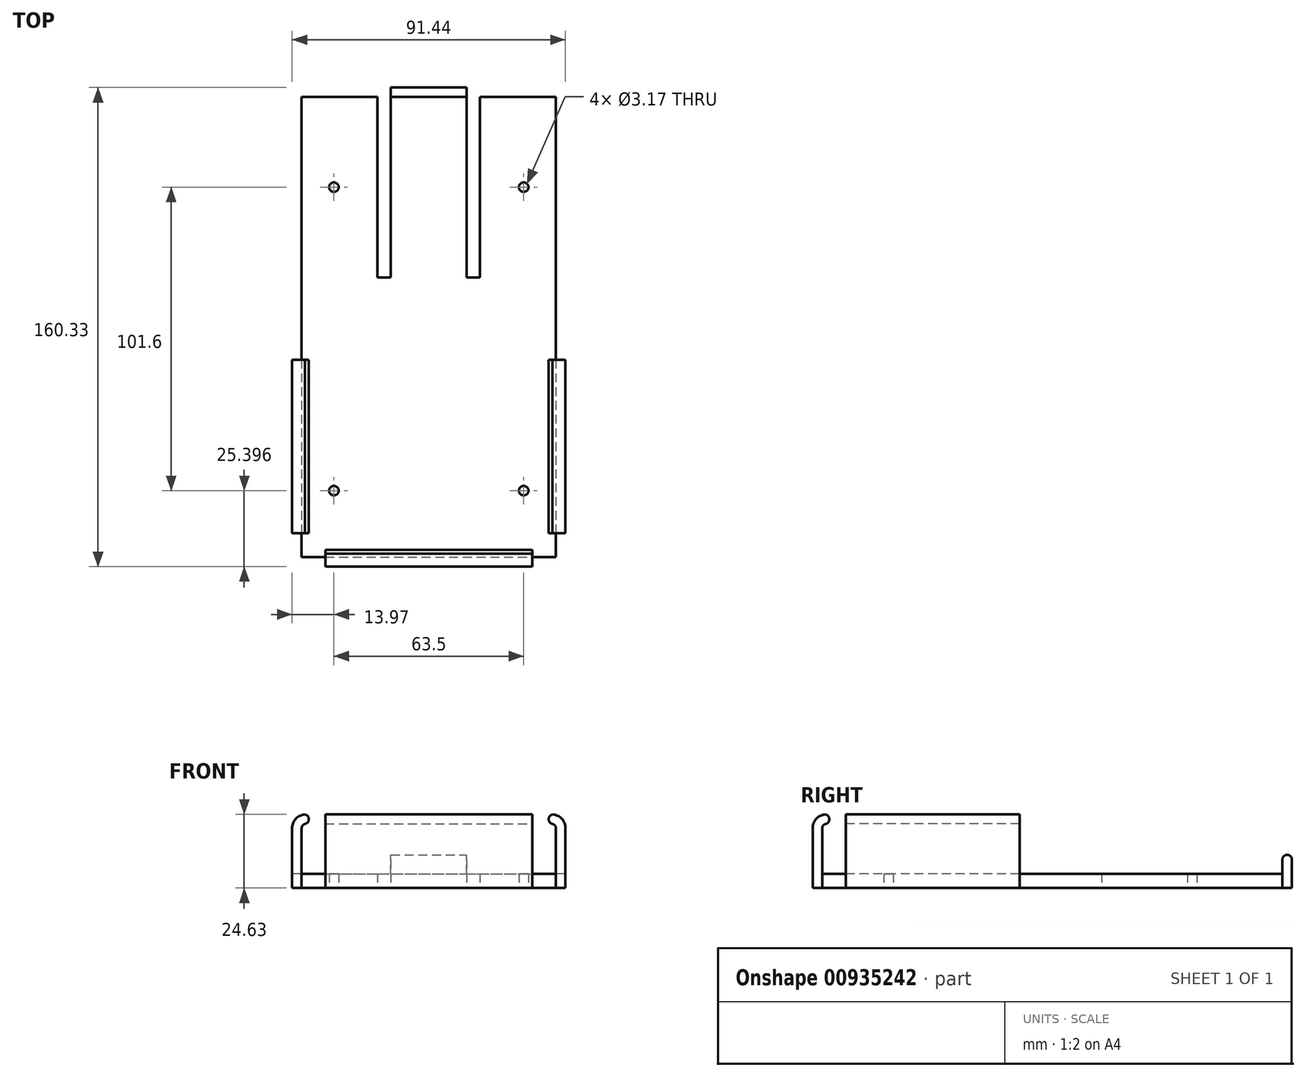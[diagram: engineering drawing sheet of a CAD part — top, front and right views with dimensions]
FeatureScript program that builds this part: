
annotation { "Feature Type Name" : "Feature", "Feature Type Description" : "" }
export const myFeature = defineFeature(function(context is Context, id is Id, definition is map)
    precondition{}
    {
        {
            var Q0;
            Q0=qCreatedBy(makeId("Top.planeOp"),FACE);
            var sketch = newSketch(context, id + "F0", { "sketchPlane" : qUnion([Q0])});
            skLineSegment(sketch, "E0.bottom", {"start": v(-42.54, 87.9) * mm, "end": v(-17.14, 87.9) * mm});
            skLineSegment(sketch, "E0.left", {"start": v(-42.54, 87.9) * mm, "end": v(-42.55, 0) * mm});
            skLineSegment(sketch, "E0.right", {"start": v(42.55, 87.9) * mm, "end": v(42.55, 0) * mm});
            skLineSegment(sketch, "E1", {"start": v(-42.55, 0) * mm, "end": v(-45.72, 0) * mm});
            skLineSegment(sketch, "E2", {"start": v(-45.72, 0) * mm, "end": v(-45.72, -58.15) * mm});
            skLineSegment(sketch, "E3", {"start": v(-45.72, -58.15) * mm, "end": v(-42.54, -58.15) * mm});
            skLineSegment(sketch, "E4", {"start": v(-34.6, -66.09) * mm, "end": v(-34.6, -69.26) * mm});
            skLineSegment(sketch, "E5", {"start": v(-34.6, -69.26) * mm, "end": v(34.6, -69.26) * mm});
            skLineSegment(sketch, "E6", {"start": v(34.6, -69.26) * mm, "end": v(34.6, -66.09) * mm});
            skLineSegment(sketch, "E7", {"start": v(42.54, -58.15) * mm, "end": v(45.72, -58.15) * mm});
            skLineSegment(sketch, "E8", {"start": v(45.72, -58.15) * mm, "end": v(45.72, 0) * mm});
            skLineSegment(sketch, "E9", {"start": v(45.72, 0) * mm, "end": v(42.55, 0) * mm});
            skLineSegment(sketch, "E10", {"start": v(-17.14, 87.9) * mm, "end": v(-17.15, 27.49) * mm});
            skLineSegment(sketch, "E11", {"start": v(-17.15, 27.49) * mm, "end": v(-12.7, 27.49) * mm});
            skLineSegment(sketch, "E12", {"start": v(17.15, 27.49) * mm, "end": v(17.15, 87.9) * mm});
            skLineSegment(sketch, "E13.trimOffspring", {"start": v(17.14, 87.9) * mm, "end": v(42.54, 87.9) * mm});
            skLineSegment(sketch, "E14", {"start": v(-12.7, 27.49) * mm, "end": v(-12.7, 91.07) * mm});
            skLineSegment(sketch, "E15", {"start": v(-12.7, 91.07) * mm, "end": v(12.7, 91.07) * mm});
            skLineSegment(sketch, "E16", {"start": v(12.7, 91.07) * mm, "end": v(12.7, 27.49) * mm});
            skLineSegment(sketch, "E17.trimOffspring", {"start": v(12.7, 27.49) * mm, "end": v(17.15, 27.49) * mm});
            skCircle(sketch, "E18", {"center": v(-31.75, -43.86) * mm, "radius": 1.59 * mm});
            skCircle(sketch, "E19", {"center": v(31.75, -43.86) * mm, "radius": 1.59 * mm});
            skCircle(sketch, "E20", {"center": v(31.75, 57.74) * mm, "radius": 1.59 * mm});
            skCircle(sketch, "E21", {"center": v(-31.75, 57.74) * mm, "radius": 1.59 * mm});
            skLineSegment(sketch, "E22", {"start": v(-42.54, -58.15) * mm, "end": v(-42.54, -66.09) * mm});
            skLineSegment(sketch, "E23", {"start": v(-42.54, -66.09) * mm, "end": v(-34.6, -66.09) * mm});
            skLineSegment(sketch, "E24", {"start": v(42.54, -58.15) * mm, "end": v(42.54, -66.09) * mm});
            skLineSegment(sketch, "E25", {"start": v(42.54, -66.09) * mm, "end": v(34.6, -66.09) * mm});
            skSolve(sketch);
        }
        {
            var Q0;
            Q0 = qSketchRegion(id + "F0", true);
            extrude(context, id + "F1", {"entities" : qUnion([Q0]), "depth" : 4.76 * mm, "offsetDistance" : 25.4 * mm});
        }
        {
            var Q0;
            Q0=makeQuery(id+"F1.opExtrude","SWEPT_FACE",FACE,{"disambiguationData":[OSD([sQuery(id+"F0.wireOp",EDGE,"E3")])]});
            var sketch = newSketch(context, id + "F2", { "sketchPlane" : qUnion([Q0])});
            skLineSegment(sketch, "E26", {"start": v(0, 0) * mm, "end": v(0, 29.09) * mm, "construction": true});
            skLineSegment(sketch, "E27", {"start": v(-45.72, 4.76) * mm, "end": v(-45.72, 4.76) * mm});
            skLineSegment(sketch, "E28", {"start": v(45.72, 4.76) * mm, "end": v(45.72, 4.76) * mm});
            skPoint(sketch, "E29.end.orphan", {"position": v(-45.72, 20) * mm});
            skPoint(sketch, "E30.MirrorCS.end.orphan", {"position": v(45.72, 20) * mm});
            skLineSegment(sketch, "E31", {"start": v(-45.72, 4.76) * mm, "end": v(-45.72, 20) * mm});
            skLineSegment(sketch, "E32", {"start": v(-42.54, 4.76) * mm, "end": v(-42.54, 20) * mm});
            skArc(sketch, "E33", {"start": v(-41.4, 24.63) * mm, "mid": v(-44.49, 23.18) * mm, "end": v(-45.72, 20) * mm});
            skArc(sketch, "E34", {"start": v(-41.4, 21.46) * mm, "mid": v(-42.23, 20.93) * mm, "end": v(-42.54, 20) * mm});
            skArc(sketch, "E35", {"start": v(-41.4, 21.46) * mm, "mid": v(-40.13, 23.05) * mm, "end": v(-41.4, 24.63) * mm});
            skLineSegment(sketch, "E36", {"start": v(-45.72, 4.76) * mm, "end": v(-42.54, 4.76) * mm});
            skLineSegment(sketch, "E37.MirrorCS", {"start": v(42.54, 4.76) * mm, "end": v(42.54, 20) * mm});
            skLineSegment(sketch, "E38.MirrorCS", {"start": v(45.72, 4.76) * mm, "end": v(45.72, 20) * mm});
            skArc(sketch, "E39.MirrorCS", {"start": v(41.4, 24.63) * mm, "mid": v(44.49, 23.18) * mm, "end": v(45.72, 20) * mm});
            skArc(sketch, "E40.MirrorCS", {"start": v(41.4, 21.46) * mm, "mid": v(42.23, 20.93) * mm, "end": v(42.54, 20) * mm});
            skArc(sketch, "E41.MirrorCS", {"start": v(41.4, 21.46) * mm, "mid": v(40.13, 23.05) * mm, "end": v(41.4, 24.63) * mm});
            skLineSegment(sketch, "E42", {"start": v(45.72, 4.76) * mm, "end": v(42.54, 4.76) * mm});
            skSolve(sketch);
        }
        {
            var Q0;
            Q0 = qSketchRegion(id + "F2", true);
            extrude(context, id + "F3", {"entities" : qUnion([Q0]), "operationType" : NewBodyOperationType.ADD, "oppositeDirection" : true, "depth" : 58.14 * mm, "offsetDistance" : 25.4 * mm});
        }
        {
            var Q0;
            Q0=makeQuery(id+"F1.opExtrude","SWEPT_FACE",FACE,{"disambiguationData":[OSD([sQuery(id+"F0.wireOp",EDGE,"E6")])]});
            var sketch = newSketch(context, id + "F4", { "sketchPlane" : qUnion([Q0])});
            skLineSegment(sketch, "E43", {"start": v(-69.26, 4.76) * mm, "end": v(-69.26, 4.76) * mm});
            skLineSegment(sketch, "E44", {"start": v(-69.26, 4.76) * mm, "end": v(-69.26, 20) * mm});
            skLineSegment(sketch, "E45", {"start": v(-66.09, 4.76) * mm, "end": v(-66.09, 20) * mm});
            skArc(sketch, "E46", {"start": v(-64.95, 21.46) * mm, "mid": v(-65.77, 20.93) * mm, "end": v(-66.09, 20) * mm});
            skArc(sketch, "E47", {"start": v(-64.95, 24.63) * mm, "mid": v(-68.03, 23.18) * mm, "end": v(-69.26, 20) * mm});
            skArc(sketch, "E48", {"start": v(-64.95, 21.46) * mm, "mid": v(-63.67, 23.05) * mm, "end": v(-64.95, 24.63) * mm});
            skLineSegment(sketch, "E49", {"start": v(-69.26, 4.76) * mm, "end": v(-66.09, 4.76) * mm});
            skSolve(sketch);
        }
        {
            var Q0;
            Q0 = qSketchRegion(id + "F4", true);
            extrude(context, id + "F5", {"entities" : qUnion([Q0]), "operationType" : NewBodyOperationType.ADD, "oppositeDirection" : true, "depth" : 69.22 * mm, "offsetDistance" : 25.4 * mm});
        }
        {
            var Q0;
            Q0=makeQuery(id+"F1.opExtrude","SWEPT_FACE",FACE,{"disambiguationData":[OSD([sQuery(id+"F0.wireOp",EDGE,"E16")])]});
            var sketch = newSketch(context, id + "F6", { "sketchPlane" : qUnion([Q0])});
            skLineSegment(sketch, "E50", {"start": v(91.07, 4.76) * mm, "end": v(91.07, 9.54) * mm});
            skLineSegment(sketch, "E51", {"start": v(87.9, 4.76) * mm, "end": v(87.9, 9.54) * mm});
            skArc(sketch, "E52", {"start": v(91.07, 9.54) * mm, "mid": v(89.49, 11.13) * mm, "end": v(87.9, 9.54) * mm});
            skLineSegment(sketch, "E53", {"start": v(87.9, 4.76) * mm, "end": v(91.07, 4.76) * mm});
            skSolve(sketch);
        }
        {
            var Q0;
            Q0 = qSketchRegion(id + "F6", true);
            extrude(context, id + "F7", {"entities" : qUnion([Q0]), "operationType" : NewBodyOperationType.ADD, "oppositeDirection" : true, "depth" : 25.4 * mm, "offsetDistance" : 25.4 * mm});
        }
    });
